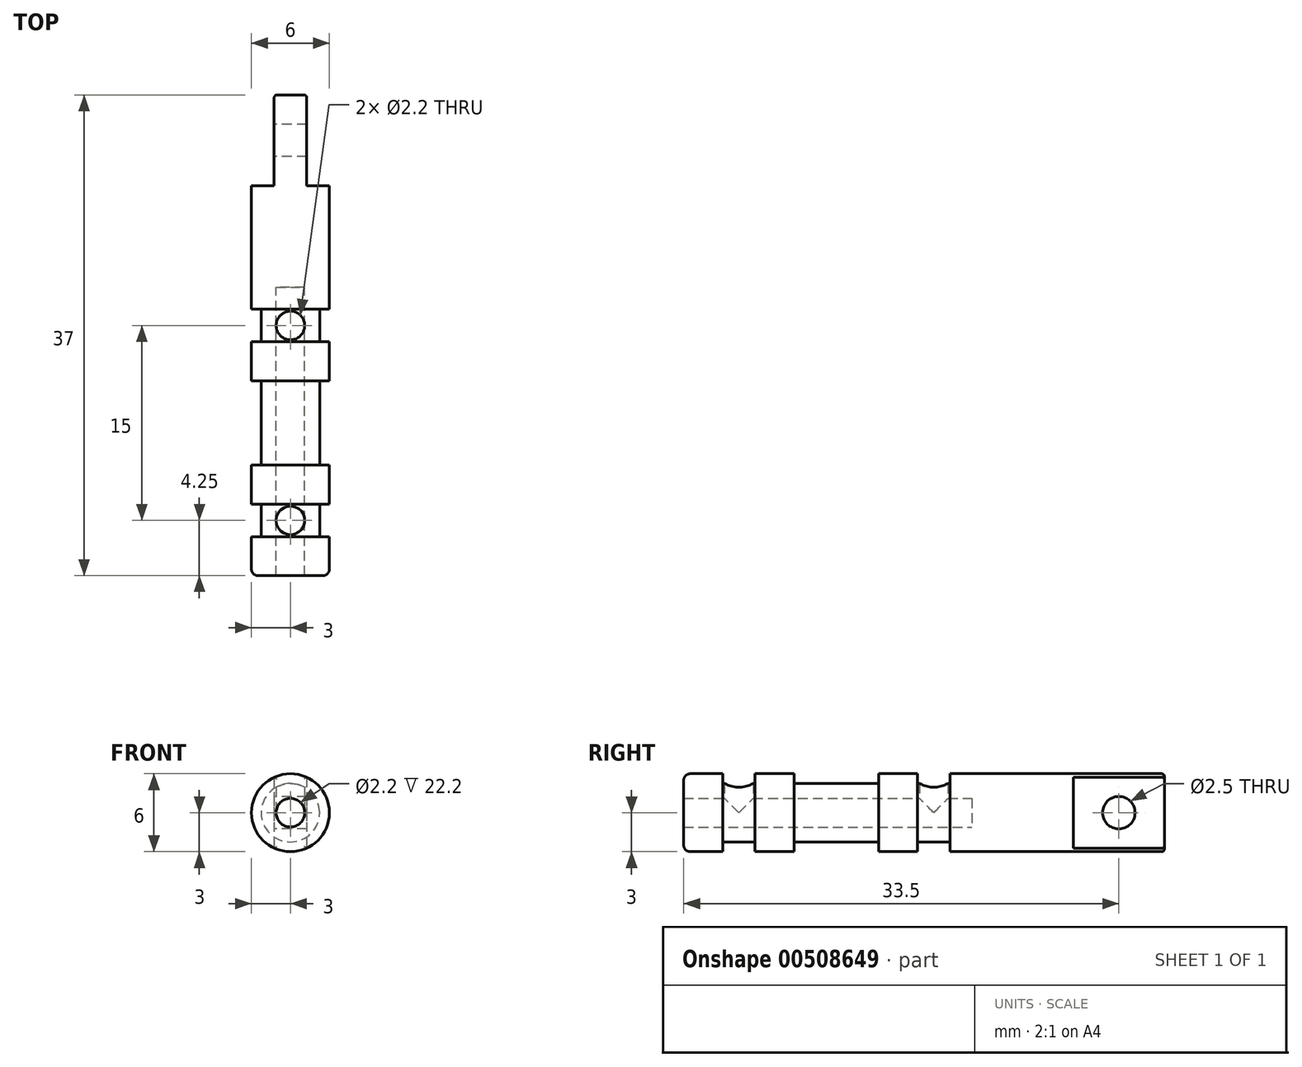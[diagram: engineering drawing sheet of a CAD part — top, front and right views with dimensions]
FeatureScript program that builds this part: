
annotation { "Feature Type Name" : "Feature", "Feature Type Description" : "" }
export const myFeature = defineFeature(function(context is Context, id is Id, definition is map)
    precondition{}
    {
        {
            var Q0;
            Q0=qCreatedBy(makeId("Front.planeOp"),FACE);
            var sketch = newSketch(context, id + "F0", { "sketchPlane" : qUnion([Q0])});
            skCircle(sketch, "E0", {"center": v(0, 0) * mm, "radius": 3 * mm});
            skCircle(sketch, "E1", {"center": v(0, 0) * mm, "radius": 1.1 * mm});
            skSolve(sketch);
        }
        {
            var Q0;
            Q0=makeQuery(id+"F0.imprint","IMPRINT",FACE,{"disambiguationData":[TD([[makeQuery(id+"F0.imprint","IMPRINT",EDGE,{"derivedFrom":sQuery(id+"F0.wireOp",EDGE,"E0")}),1.0]])]});
            extrude(context, id + "F1", {"entities" : qUnion([Q0]), "depth" : 3 * mm});
        }
        {
            var Q0;
            Q0=qCreatedBy(makeId("Front.planeOp"),FACE);
            var sketch = newSketch(context, id + "F2", { "sketchPlane" : qUnion([Q0])});
            skCircle(sketch, "E2", {"center": v(0, 0) * mm, "radius": 2.25 * mm});
            skLineSegment(sketch, "E3", {"start": v(2.25, 0) * mm, "end": v(-2.25, 0) * mm, "construction": true});
            skLineSegment(sketch, "E4", {"start": v(0, 2.25) * mm, "end": v(0, -2.25) * mm, "construction": true});
            skSolve(sketch);
        }
        {
            var Q0;
            Q0=makeQuery(id+"F2.imprint","IMPRINT",FACE,{"disambiguationData":[TD([[makeQuery(id+"F2.imprint","IMPRINT",EDGE,{"derivedFrom":sQuery(id+"F2.wireOp",EDGE,"E2")}),1.0]])]});
            extrude(context, id + "F3", {"entities" : qUnion([Q0]), "operationType" : NewBodyOperationType.ADD, "oppositeDirection" : true, "depth" : 2.5 * mm});
        }
        {
            var Q0;
            Q0=makeQuery(id+"F3.opExtrude","CAP_FACE",FACE,{"disambiguationData":[OSD([sQuery(id+"F2.wireOp",EDGE,"E2")])],"isStart":false});
            var sketch = newSketch(context, id + "F4", { "sketchPlane" : qUnion([Q0])});
            skLineSegment(sketch, "E5", {"start": v(-2.25, 0) * mm, "end": v(2.25, 0) * mm, "construction": true});
            skLineSegment(sketch, "E6", {"start": v(0, 2.25) * mm, "end": v(0, -2.25) * mm, "construction": true});
            skPoint(sketch, "E7", {"position": v(0, 0) * mm});
            skSolve(sketch);
        }
        {
            var Q0;
            Q0=makeQuery(id+"F1.opExtrude","CAP_EDGE",EDGE,{"disambiguationData":[OSD([sQuery(id+"F0.wireOp",EDGE,"E0")])],"isStart":false});
            fillet(context, id + "F5", {"entities" : qUnion([Q0]), "radius" : 0.5 * mm, "tangentPropagation" : true, "allowEdgeOverflow" : false});
        }
        {
            var Q0;
            Q0=sQuery(id+"F4.wireOp",EDGE,"E5");
            cPoint(context, id + "F6", {"entities" : qUnion([Q0]), "parameter" : 0.5});
        }
        {
            var Q0;
            Q0=qCreatedBy(makeId("Front.planeOp"),FACE);
            var Q1;
            Q1 = qCreatedBy(id + "F6" ,VERTEX);
            cPlane(context, id + "F7", {"entities" : qUnion([Q0, Q1]), "cplaneType" : CPlaneType.PLANE_POINT, "offset" : 25 * mm, "width" : 150 * mm, "height" : 150 * mm});
        }
        {
            var Q0;
            Q0=qCreatedBy(id+"F7.planeOp",FACE);
            var sketch = newSketch(context, id + "F8", { "sketchPlane" : qUnion([Q0])});
            skCircle(sketch, "E8", {"center": v(0, 0) * mm, "radius": 3 * mm});
            skSolve(sketch);
        }
        {
            var Q0;
            Q0 = qSketchRegion(id + "F8", true);
            extrude(context, id + "F9", {"entities" : qUnion([Q0]), "operationType" : NewBodyOperationType.ADD, "oppositeDirection" : true, "depth" : 3 * mm});
        }
        {
            var Q0;
            Q0=makeQuery(id+"F9.opExtrude","CAP_FACE",FACE,{"disambiguationData":[OSD([sQuery(id+"F8.wireOp",EDGE,"E8")])],"isStart":false});
            cPlane(context, id + "F10", {"entities" : qUnion([Q0]), "cplaneType" : CPlaneType.OFFSET, "offset" : 0 * mm, "width" : 150 * mm, "height" : 150 * mm});
        }
        {
            var Q0;
            Q0=qCreatedBy(id+"F10.planeOp",FACE);
            var sketch = newSketch(context, id + "F11", { "sketchPlane" : qUnion([Q0])});
            skCircle(sketch, "E9", {"center": v(0, 0) * mm, "radius": 2.25 * mm});
            skSolve(sketch);
        }
        {
            var Q0;
            Q0=makeQuery(id+"F11.imprint","IMPRINT",FACE,{"disambiguationData":[TD([[makeQuery(id+"F11.imprint","IMPRINT",EDGE,{"derivedFrom":sQuery(id+"F11.wireOp",EDGE,"E9")}),1.0]])]});
            extrude(context, id + "F12", {"entities" : qUnion([Q0]), "operationType" : NewBodyOperationType.ADD, "depth" : 6.5 * mm});
        }
        {
            var Q0;
            Q0=makeQuery(id+"F12.opExtrude","CAP_FACE",FACE,{"disambiguationData":[OSD([sQuery(id+"F11.wireOp",EDGE,"E9")])],"isStart":false});
            cPlane(context, id + "F13", {"entities" : qUnion([Q0]), "cplaneType" : CPlaneType.OFFSET, "offset" : 0 * mm, "width" : 150 * mm, "height" : 150 * mm});
        }
        {
            var Q0;
            Q0=qCreatedBy(id+"F13.planeOp",FACE);
            var sketch = newSketch(context, id + "F14", { "sketchPlane" : qUnion([Q0])});
            skCircle(sketch, "E10", {"center": v(0, 0) * mm, "radius": 3 * mm});
            skSolve(sketch);
        }
        {
            var Q0;
            Q0=makeQuery(id+"F14.imprint","IMPRINT",FACE,{"disambiguationData":[TD([[makeQuery(id+"F14.imprint","IMPRINT",EDGE,{"derivedFrom":sQuery(id+"F14.wireOp",EDGE,"E10")}),1.0]])]});
            extrude(context, id + "F15", {"entities" : qUnion([Q0]), "operationType" : NewBodyOperationType.ADD, "depth" : 3 * mm});
        }
        {
            var Q0;
            Q0=makeQuery(id+"F15.opExtrude","CAP_FACE",FACE,{"disambiguationData":[OSD([sQuery(id+"F14.wireOp",EDGE,"E10")])],"isStart":false});
            cPlane(context, id + "F16", {"entities" : qUnion([Q0]), "cplaneType" : CPlaneType.OFFSET, "offset" : 0 * mm, "width" : 150 * mm, "height" : 150 * mm});
        }
        {
            var Q0;
            Q0=qCreatedBy(id+"F16.planeOp",FACE);
            var sketch = newSketch(context, id + "F17", { "sketchPlane" : qUnion([Q0])});
            skCircle(sketch, "E11", {"center": v(0, 0) * mm, "radius": 2.25 * mm});
            skSolve(sketch);
        }
        {
            var Q0;
            Q0=makeQuery(id+"F17.imprint","IMPRINT",FACE,{"disambiguationData":[TD([[makeQuery(id+"F17.imprint","IMPRINT",EDGE,{"derivedFrom":sQuery(id+"F17.wireOp",EDGE,"E11")}),1.0]])]});
            extrude(context, id + "F18", {"entities" : qUnion([Q0]), "operationType" : NewBodyOperationType.ADD, "depth" : 2.5 * mm});
        }
        {
            var Q0;
            Q0=makeQuery(id+"F18.opExtrude","CAP_FACE",FACE,{"disambiguationData":[OSD([sQuery(id+"F17.wireOp",EDGE,"E11")])],"isStart":false});
            cPlane(context, id + "F19", {"entities" : qUnion([Q0]), "cplaneType" : CPlaneType.OFFSET, "offset" : 0 * mm, "width" : 150 * mm, "height" : 150 * mm});
        }
        {
            var Q0;
            Q0=qCreatedBy(id+"F19.planeOp",FACE);
            var sketch = newSketch(context, id + "F20", { "sketchPlane" : qUnion([Q0])});
            skCircle(sketch, "E12", {"center": v(0, 0) * mm, "radius": 3 * mm});
            skSolve(sketch);
        }
        {
            var Q0;
            Q0=makeQuery(id+"F20.imprint","IMPRINT",FACE,{"disambiguationData":[TD([[makeQuery(id+"F20.imprint","IMPRINT",EDGE,{"derivedFrom":sQuery(id+"F20.wireOp",EDGE,"E12")}),1.0]])]});
            extrude(context, id + "F21", {"entities" : qUnion([Q0]), "operationType" : NewBodyOperationType.ADD, "depth" : 9.5 * mm});
        }
        {
            var Q0;
            Q0=makeQuery(id+"F21.opExtrude","CAP_FACE",FACE,{"disambiguationData":[OSD([sQuery(id+"F20.wireOp",EDGE,"E12")])],"isStart":false});
            cPlane(context, id + "F22", {"entities" : qUnion([Q0]), "cplaneType" : CPlaneType.OFFSET, "offset" : 0 * mm, "width" : 150 * mm, "height" : 150 * mm});
        }
        {
            var Q0;
            Q0=qCreatedBy(id+"F22.planeOp",FACE);
            var sketch = newSketch(context, id + "F23", { "sketchPlane" : qUnion([Q0])});
            skPoint(sketch, "E13", {"position": v(0, 0) * mm});
            skLineSegment(sketch, "E14", {"start": v(-1.25, 0) * mm, "end": v(1.25, 0) * mm, "construction": true});
            skLineSegment(sketch, "E15", {"start": v(-1.25, 2.73) * mm, "end": v(-1.25, -2.73) * mm});
            skLineSegment(sketch, "E16", {"start": v(1.25, 2.73) * mm, "end": v(1.25, -2.73) * mm});
            skArc(sketch, "E17", {"start": v(-1.25, 2.73) * mm, "mid": v(0, 3) * mm, "end": v(1.25, 2.73) * mm});
            skArc(sketch, "E18", {"start": v(-1.25, -2.73) * mm, "mid": v(0, -3) * mm, "end": v(1.25, -2.73) * mm});
            skSolve(sketch);
        }
        {
            var Q0;
            Q0=makeQuery(id+"F23.imprint","IMPRINT",FACE,{"disambiguationData":[TD([[makeQuery(id+"F23.imprint","IMPRINT",EDGE,{"derivedFrom":sQuery(id+"F23.wireOp",EDGE,"E15")}),1.0]])]});
            extrude(context, id + "F24", {"entities" : qUnion([Q0]), "operationType" : NewBodyOperationType.ADD, "depth" : 7 * mm});
        }
        {
            var Q0;
            Q0=sQuery(id+"F4.wireOp",VERTEX,"E7");
            var Q1;
            Q1=makeQuery(id+"F1.opExtrude","SWEPT_BODY",BODY,{"disambiguationData":[OSD([sQuery(id+"F0.wireOp",EDGE,"E0"),sQuery(id+"F0.wireOp",EDGE,"E1")])]});
            hole(context, id + "F25", {"style" : HoleStyle.SIMPLE, "endStyle" : HoleEndStyle.BLIND, "holeDiameter" : 2.2 * mm, "holeDepth" : 23 * mm, "isTappedThrough" : true, "tappedDepth" : 12 * mm, "tapClearance" : 3, "locations" : qUnion([Q0]), "scope" : qUnion([Q1])});
        }
        {
            var Q0;
            Q0=qCreatedBy(makeId("Right.planeOp"),FACE);
            var sketch = newSketch(context, id + "F26", { "sketchPlane" : qUnion([Q0])});
            skPoint(sketch, "E19", {"position": v(30.5, 0) * mm});
            skCircle(sketch, "E20", {"center": v(30.5, 0) * mm, "radius": 1.25 * mm});
            skSolve(sketch);
        }
        {
            var Q0;
            Q0=sQuery(id+"F26.wireOp",VERTEX,"E19");
            var Q1;
            Q1=makeQuery(id+"F1.opExtrude","SWEPT_BODY",BODY,{"disambiguationData":[OSD([sQuery(id+"F0.wireOp",EDGE,"E0"),sQuery(id+"F0.wireOp",EDGE,"E1")])]});
            hole(context, id + "F27", {"style" : HoleStyle.SIMPLE, "endStyle" : HoleEndStyle.BLIND, "oppositeDirection" : true, "holeDiameter" : 2.5 * mm, "holeDepth" : 7 * mm, "isTappedThrough" : true, "tappedDepth" : 12 * mm, "tapClearance" : 3, "locations" : qUnion([Q0]), "scope" : qUnion([Q1])});
        }
        {
            var Q0;
            Q0=makeQuery(id+"F24.opExtrude","SWEPT_FACE",FACE,{"disambiguationData":[OSD([sQuery(id+"F23.wireOp",EDGE,"E16")])]});
            var sketch = newSketch(context, id + "F28", { "sketchPlane" : qUnion([Q0])});
            skLineSegment(sketch, "E21", {"start": v(-30.5, 2.73) * mm, "end": v(-30.5, -2.73) * mm, "construction": true});
            skPoint(sketch, "E22", {"position": v(-30.5, 0) * mm});
            skSolve(sketch);
        }
        {
            var Q0;
            Q0=sQuery(id+"F28.wireOp",VERTEX,"E22");
            var Q1;
            Q1=makeQuery(id+"F1.opExtrude","SWEPT_BODY",BODY,{"disambiguationData":[OSD([sQuery(id+"F0.wireOp",EDGE,"E0"),sQuery(id+"F0.wireOp",EDGE,"E1")])]});
            hole(context, id + "F29", {"style" : HoleStyle.SIMPLE, "endStyle" : HoleEndStyle.BLIND, "holeDiameter" : 2.5 * mm, "holeDepth" : 7 * mm, "isTappedThrough" : true, "tappedDepth" : 12 * mm, "tapClearance" : 3, "locations" : qUnion([Q0]), "scope" : qUnion([Q1])});
        }
        {
            var Q0;
            Q0=qCreatedBy(makeId("Top.planeOp"),FACE);
            var sketch = newSketch(context, id + "F30", { "sketchPlane" : qUnion([Q0])});
            skPoint(sketch, "E23", {"position": v(0, 1.25) * mm});
            skCircle(sketch, "E24", {"center": v(0, 1.25) * mm, "radius": 1.1 * mm});
            skPoint(sketch, "E25", {"position": v(0, 16.25) * mm});
            skCircle(sketch, "E26", {"center": v(0, 16.25) * mm, "radius": 1.1 * mm});
            skSolve(sketch);
        }
        {
            var Q0;
            Q0=sQuery(id+"F30.wireOp",VERTEX,"E24.center");
            var Q1;
            Q1=sQuery(id+"F30.wireOp",VERTEX,"E25");
            var Q2;
            Q2=makeQuery(id+"F1.opExtrude","SWEPT_BODY",BODY,{"disambiguationData":[OSD([sQuery(id+"F0.wireOp",EDGE,"E0"),sQuery(id+"F0.wireOp",EDGE,"E1")])]});
            hole(context, id + "F31", {"style" : HoleStyle.SIMPLE, "endStyle" : HoleEndStyle.BLIND, "oppositeDirection" : true, "holeDiameter" : 2.2 * mm, "holeDepth" : 3 * mm, "isTappedThrough" : true, "tappedDepth" : 12 * mm, "tapClearance" : 3, "startFromSketch" : true, "locations" : qUnion([Q0, Q1]), "scope" : qUnion([Q2])});
        }
        {
            var Q0;
            Q0=makeQuery(id+"F21.opExtrude","CAP_FACE",FACE,{"disambiguationData":[OSD([sQuery(id+"F20.wireOp",EDGE,"E12")])],"isStart":true});
            cPlane(context, id + "F32", {"entities" : qUnion([Q0]), "cplaneType" : CPlaneType.OFFSET, "offset" : 1.7 * mm, "oppositeDirection" : true, "width" : 150 * mm, "height" : 150 * mm});
        }
        {
            var Q0;
            Q0=qCreatedBy(id+"F32.planeOp",FACE);
            var sketch = newSketch(context, id + "F33", { "sketchPlane" : qUnion([Q0])});
            skLineSegment(sketch, "E27", {"start": v(-1.44, 0) * mm, "end": v(1.3, 0) * mm, "construction": true});
            skLineSegment(sketch, "E28", {"start": v(0, 1.36) * mm, "end": v(0, -1.37) * mm, "construction": true});
            skPoint(sketch, "E29", {"position": v(0, 0) * mm});
            skSolve(sketch);
        }
        {
            var Q0;
            Q0=sQuery(id+"F33.wireOp",VERTEX,"E29");
            var Q1;
            Q1=makeQuery(id+"F1.opExtrude","SWEPT_BODY",BODY,{"disambiguationData":[OSD([sQuery(id+"F0.wireOp",EDGE,"E0"),sQuery(id+"F0.wireOp",EDGE,"E1")])]});
            hole(context, id + "F34", {"style" : HoleStyle.SIMPLE, "endStyle" : HoleEndStyle.BLIND, "oppositeDirection" : true, "holeDiameter" : 2.2 * mm, "holeDepth" : 23 * mm, "isTappedThrough" : true, "tappedDepth" : 12 * mm, "tapClearance" : 3, "startFromSketch" : true, "locations" : qUnion([Q0]), "scope" : qUnion([Q1])});
        }
        {
            var Q0;
            Q0=makeQuery(id+"F24.opExtrude","CAP_EDGE",EDGE,{"disambiguationData":[OSD([sQuery(id+"F23.wireOp",EDGE,"E15")])],"isStart":false});
            var Q1;
            Q1=makeQuery(id+"F24.opExtrude","CAP_EDGE",EDGE,{"disambiguationData":[OSD([sQuery(id+"F23.wireOp",EDGE,"E16")])],"isStart":false});
            var Q2;
            Q2=makeQuery(id+"F24.opExtrude","CAP_EDGE",EDGE,{"disambiguationData":[OSD([sQuery(id+"F23.wireOp",EDGE,"E18")])],"isStart":false});
            var Q3;
            Q3=makeQuery(id+"F24.opExtrude","CAP_EDGE",EDGE,{"disambiguationData":[OSD([sQuery(id+"F23.wireOp",EDGE,"E17")])],"isStart":false});
            fillet(context, id + "F35", {"entities" : qUnion([Q0, Q1, Q2, Q3]), "radius" : 0.2 * mm, "tangentPropagation" : true, "allowEdgeOverflow" : false});
        }
    });
